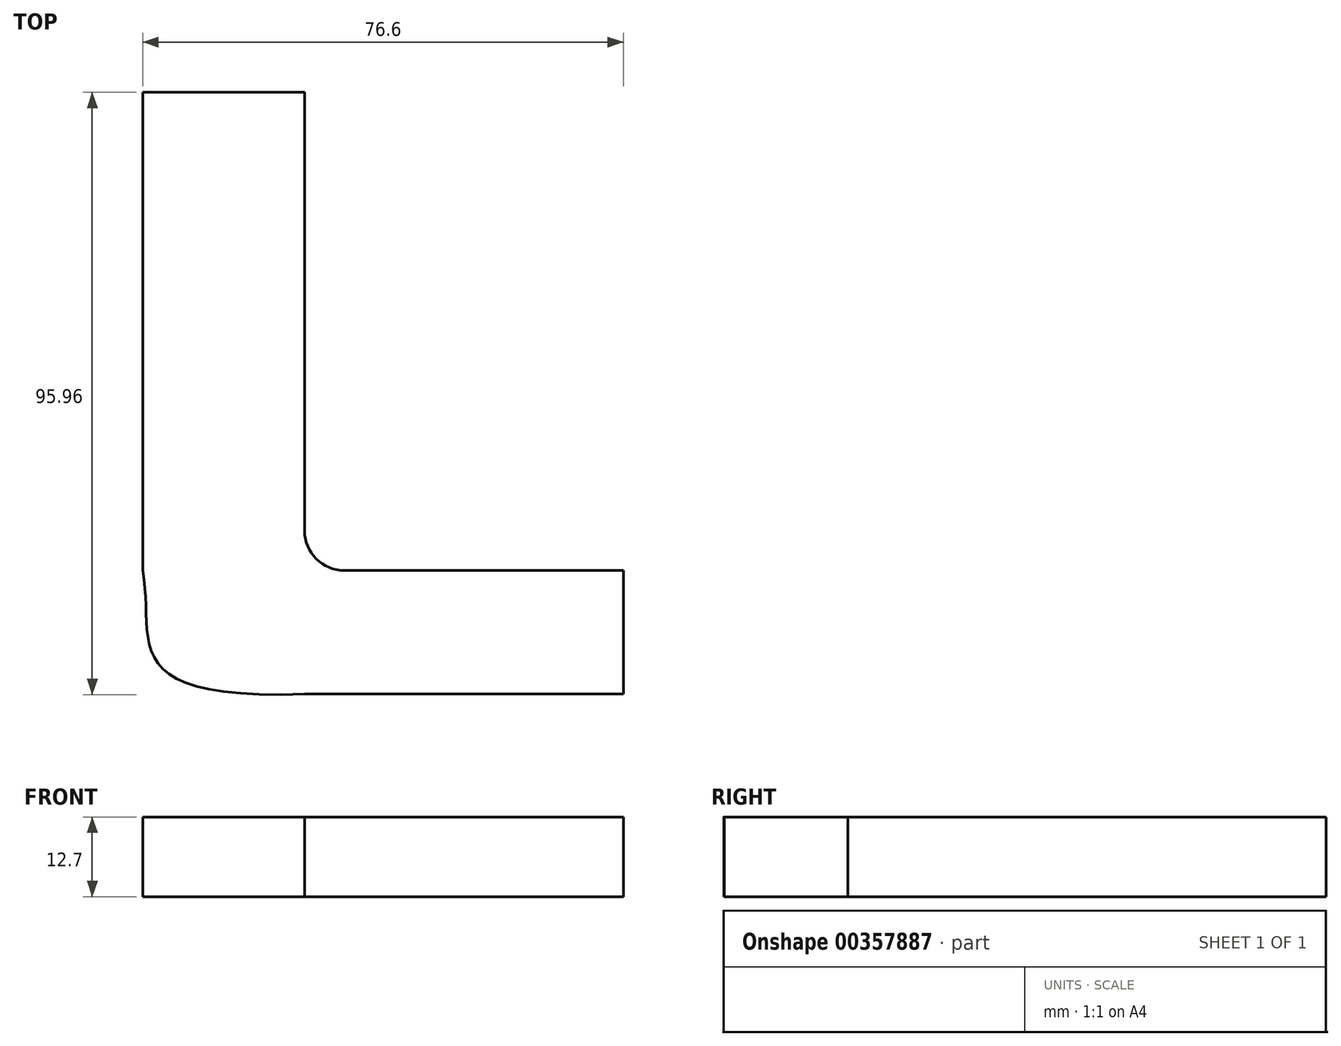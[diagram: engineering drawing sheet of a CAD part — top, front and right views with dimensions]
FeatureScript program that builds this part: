
annotation { "Feature Type Name" : "Feature", "Feature Type Description" : "" }
export const myFeature = defineFeature(function(context is Context, id is Id, definition is map)
    precondition{}
    {
        {
            var Q0;
            Q0=qCreatedBy(makeId("Top.planeOp"),FACE);
            var sketch = newSketch(context, id + "F0", { "sketchPlane" : qUnion([Q0])});
            skLineSegment(sketch, "E0.bottom", {"start": v(0, 0) * mm, "end": v(-25.8, 0) * mm});
            skLineSegment(sketch, "E0.top", {"start": v(0, 76.2) * mm, "end": v(-25.8, 76.2) * mm});
            skLineSegment(sketch, "E0.left", {"start": v(0, 6.35) * mm, "end": v(0, 76.2) * mm});
            skLineSegment(sketch, "E0.right", {"start": v(-25.8, 0) * mm, "end": v(-25.8, 76.2) * mm});
            skLineSegment(sketch, "E1.bottom", {"start": v(6.35, 0) * mm, "end": v(50.8, 0) * mm});
            skLineSegment(sketch, "E1.top", {"start": v(0, -19.68) * mm, "end": v(50.8, -19.68) * mm});
            skLineSegment(sketch, "E1.left", {"start": v(0, 0) * mm, "end": v(0, -19.68) * mm});
            skLineSegment(sketch, "E1.right", {"start": v(50.8, 0) * mm, "end": v(50.8, -19.68) * mm});
            skFitSpline(sketch, "E2", {"points": [v(-25.8, 0) * mm, v(0, -19.68) * mm], "startDerivative": vector(6.38, -32.71) * mm, "endDerivative": vector(92.56, 3.2) * mm});
            skPoint(sketch, "E3.visualSharp", {"position": v(0, 0) * mm});
            skArc(sketch, "E3.filletArc", {"start": v(0, 6.35) * mm, "mid": v(1.86, 1.86) * mm, "end": v(6.35, 0) * mm});
            skSolve(sketch);
        }
        {
            var Q0;
            Q0 = qSketchRegion(id + "F0", true);
            extrude(context, id + "F1", {"entities" : qUnion([Q0]), "depth" : 12.7 * mm});
        }
    });
